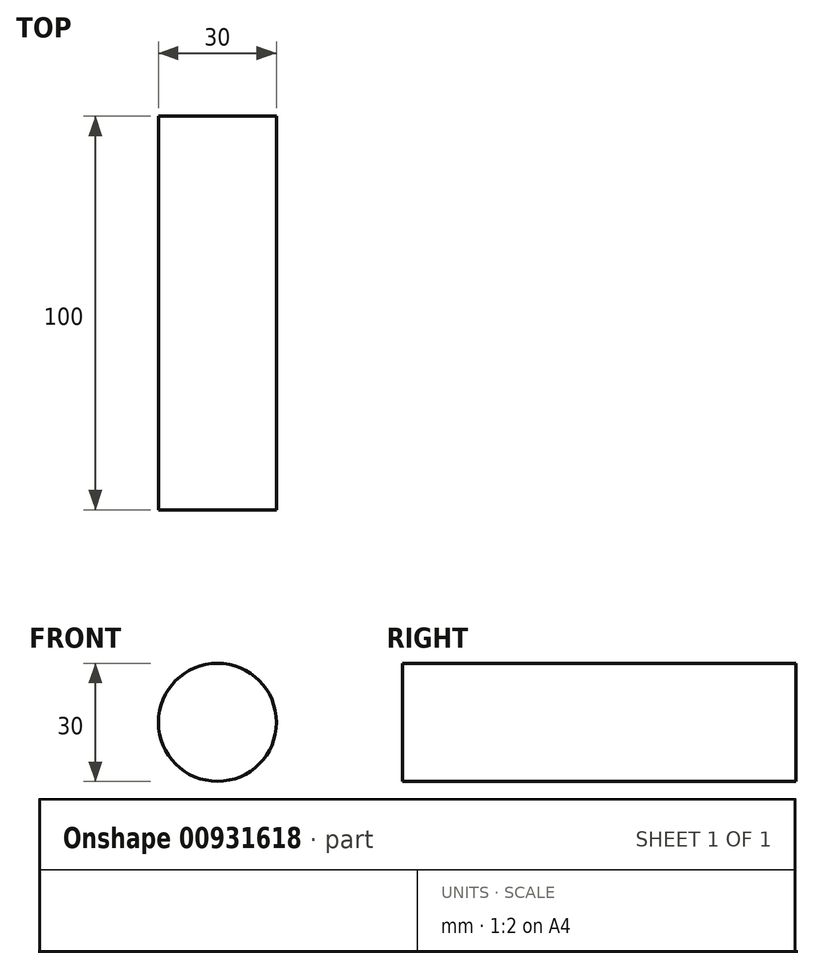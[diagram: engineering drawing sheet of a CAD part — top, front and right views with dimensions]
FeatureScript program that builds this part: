
annotation { "Feature Type Name" : "Feature", "Feature Type Description" : "" }
export const myFeature = defineFeature(function(context is Context, id is Id, definition is map)
    precondition{}
    {
        {
            var Q0;
            Q0=qCreatedBy(makeId("Front.planeOp"),FACE);
            var sketch = newSketch(context, id + "F0", { "sketchPlane" : qUnion([Q0])});
            skCircle(sketch, "E0", {"center": v(-2.92, 0) * mm, "radius": 15 * mm});
            skSolve(sketch);
        }
        {
            var Q0;
            Q0 = qSketchRegion(id + "F0", true);
            extrude(context, id + "F1", {"entities" : qUnion([Q0]), "endBound" : BoundingType.SYMMETRIC, "depth" : 100 * mm, "offsetDistance" : 25.4 * mm});
        }
    });
